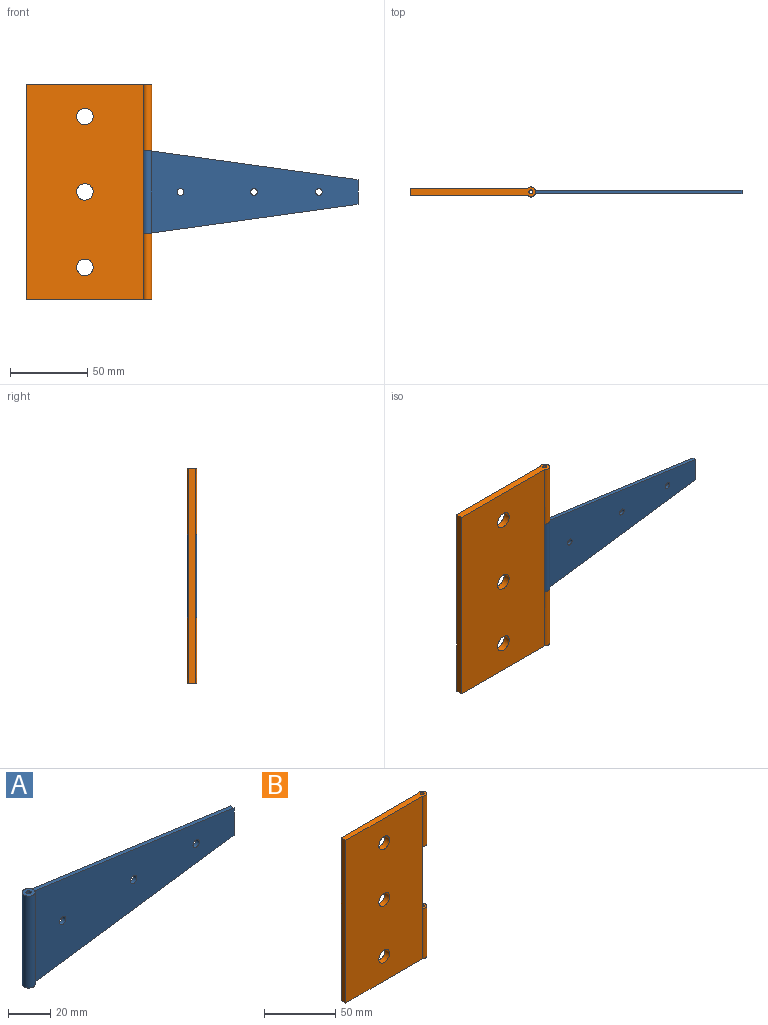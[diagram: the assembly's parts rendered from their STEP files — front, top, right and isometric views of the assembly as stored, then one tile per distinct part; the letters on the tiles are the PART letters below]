
ASSEMBLY  parts=2 mates=1
PART A: 12 faces, bbox 139.7x6.3x53.4 mm
  f0: plane 6.29x6.29mm, normal (0,0,1), area 26mm2, adj f1,f11
  f1: cylinder r=3.15mm len=53.34mm, axis (0,0,1), area 930.5mm2, adj f0,f2,f3,f4,f9,f10
  f2: plane 6.29x6.29mm, normal (0,0,-1), area 26mm2, adj f1,f11
  f3: plane 133.64x18.57mm, normal (0.14,0,0.99), area 308.1mm2, adj f1,f8,f9,f10
  f4: plane 133.64x18.57mm, normal (0.14,0,-0.99), area 308.1mm2, adj f1,f8,f9,f10
  f5: cylinder r=2.16mm len=4.32mm, axis (0,1,0), area 31mm2, adj f9,f10
  f6: cylinder r=2.16mm len=4.32mm, axis (0,1,0), area 31mm2, adj f9,f10
  f7: cylinder r=2.16mm len=4.32mm, axis (0,1,0), area 31mm2, adj f9,f10
  f8: plane 15.97x2.29mm, normal (1,0,0), area 36.5mm2, adj f3,f4,f9,f10
  f9: plane 133.62x53.09mm, normal (0,-1,0), area 4570.2mm2, adj f1,f3,f4,f5,f6,f7,f8
  f10: plane 133.62x53.09mm, normal (0,1,0), area 4570.2mm2, adj f1,f3,f4,f5,f6,f7,f8
  f11: cylinder r=1.27mm len=53.34mm, axis (0,0,-1), area 425.6mm2, adj f0,f2
PART B: 14 faces, bbox 81.4x6.3x139.7 mm
  f0: cylinder r=3.15mm len=139.7mm, axis (0,0,-1), area 1268.1mm2, adj f2,f4,f8,f9,f11,f12,f13
  f1: cylinder r=1.27mm len=43.18mm, axis (0,0,-1), area 344.6mm2, adj f2,f11
  f2: plane 81.37x6.29mm, normal (0,0,1), area 370.7mm2, adj f0,f1,f3,f8,f9
  f3: plane 139.7x4.57mm, normal (-1,0,0), area 638.7mm2, adj f2,f4,f8,f9
  f4: plane 81.37x6.29mm, normal (0,0,-1), area 370.7mm2, adj f0,f3,f8,f9,f10
  f5: cylinder r=5.33mm len=10.67mm, axis (0,1,0), area 153.2mm2, adj f8,f9
  f6: cylinder r=5.33mm len=10.67mm, axis (0,1,0), area 153.2mm2, adj f8,f9
  f7: cylinder r=5.33mm len=10.67mm, axis (0,1,0), area 153.2mm2, adj f8,f9
  f8: plane 139.7x76.06mm, normal (0,-1,0), area 10357.7mm2, adj f0,f2,f3,f4,f5,f6,f7
  f9: plane 139.7x76.06mm, normal (0,1,0), area 10357.7mm2, adj f0,f2,f3,f4,f5,f6,f7
  f10: cylinder r=1.27mm len=43.18mm, axis (0,0,-1), area 344.6mm2, adj f4,f12
  f11: plane 6.29x5.29mm, normal (0,0,-1), area 22.8mm2, adj f0,f1,f13
  f12: plane 6.29x5.29mm, normal (0,0,1), area 22.8mm2, adj f0,f10,f13
  f13: plane 53.34x4.61mm, normal (1,0,0), area 245.7mm2, adj f0,f11,f12
PLACE A rot(axis=(0,0,1),0deg) t=(22.8,7.04,27.94)mm
PLACE B t=(-56.53,9.32,31.82)mm fixed
MATE revolute A.f1 <-> B.f0  axis (0,0,-1) through (-23.34,7.04,-4.55)mm
